# Revit family: Storage-Mounted-Teknion-JNMELF-Overlay_Sliding_Fabric_Door-R2018
name_source: partatom
category: Furniture
revit_build: Autodesk Revit 2018 (Build: 20190510_1515(x64)
units: mm (PartAtom-declared; Revit-internal decimal feet)

## family parameters
Always vertical = Yes
Cut with Voids When Loaded = No
OmniClass Number = 23.40.20.00
OmniClass Title = General Furniture and Specialties
Room Calculation Point = No
Shared = Yes
Work Plane-Based = No

## types (3) — shared parameters
Assembly Code = E2020200
Manufacturer = Teknion
Manufacturer Fax = 416.661.4586
Part Number = JNMELF
Product Documentation Link = https://www.teknion.com
Product Line = Cityline
Product Page URL = https://www.teknion.com
Series = Cityline
Sustainability Data = http://www.teknion.com
URL = www.teknion.com
Unit Weight URL = http://www.teknion.com
Warranty = http://www.teknion.com

## per-type parameters (varying)
| type | 2D Visibility for Back Gable | 2D Visibility for Right Door | Back Face of Middle Divider Offset | Description | Left Door Hole Depth | Model | Shared | Single-Sided - Two Doors Hole Depth | Single-Sided - Two Doors Lock Hole Depth |
| Shared | No | Yes | 1.567 " | Elevated Cabinet – Overlay Sliding Door – Fabric, Angled, for Datum Height 51", Shared | 18.511 " | JNMELFA22_D_ | Yes | 3.866 " | 2.5 " |
| Single-Sided - One Door | Yes | No | 0.701 " | Elevated Cabinet – Overlay Sliding Door – Fabric, Angled, for Datum Height 51", Single-Sided - One Door | 17.81 " | JNMELFA22_O_ | No | 17.81 " | 2.5 " |
| Single-Sided - Two Doors | Yes | Yes | 0.701 " | Elevated Cabinet – Overlay Sliding Door – Fabric, Angled, for Datum Height 51", Single-Sided - Two Doors | 17.81 " | JNMELFA22_T_ | No | 17.81 " | 4.534 " |

type visibility flags (boolean, named after types; folded from table):
- Shared: Yes: (none)
- Single-Sided - One Door: Yes: Single-Sided - One Door
- Single-Sided - Two Doors: Yes: Single-Sided - Two Doors

## geometry (parser evidence)
native form markers: Sweep x2
no freeform markers — native parametric forms only
